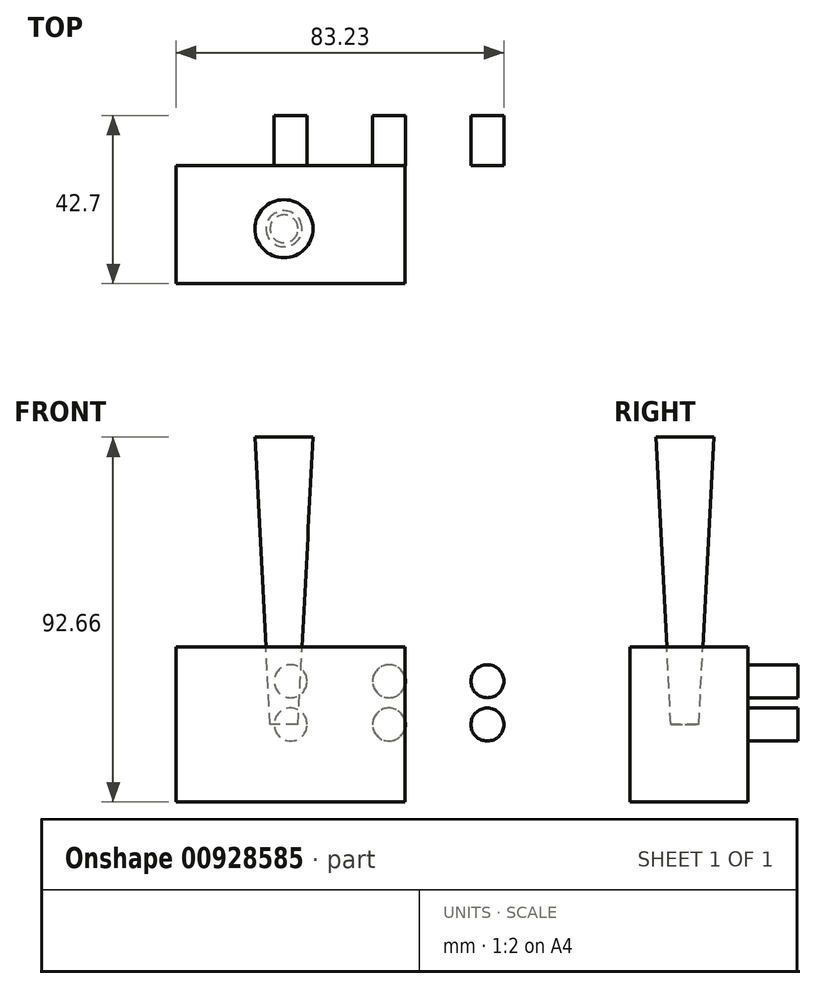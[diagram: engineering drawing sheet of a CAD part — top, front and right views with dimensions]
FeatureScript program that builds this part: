
annotation { "Feature Type Name" : "Feature", "Feature Type Description" : "" }
export const myFeature = defineFeature(function(context is Context, id is Id, definition is map)
    precondition{}
    {
        {
            var Q0;
            Q0=qCreatedBy(makeId("Front.planeOp"),FACE);
            var sketch = newSketch(context, id + "F0", { "sketchPlane" : qUnion([Q0])});
            skLineSegment(sketch, "E0.bottom", {"start": v(29.04, -19.66) * mm, "end": v(-29.04, -19.66) * mm});
            skLineSegment(sketch, "E0.top", {"start": v(29.04, 19.66) * mm, "end": v(-29.04, 19.66) * mm});
            skLineSegment(sketch, "E0.left", {"start": v(29.04, -19.66) * mm, "end": v(29.04, 19.66) * mm});
            skLineSegment(sketch, "E0.right", {"start": v(-29.04, -19.66) * mm, "end": v(-29.04, 19.66) * mm});
            skPoint(sketch, "E0.middle", {"position": v(0, 0) * mm});
            skSolve(sketch);
        }
        {
            var Q0;
            Q0 = qSketchRegion(id + "F0", true);
            extrude(context, id + "F1", {"entities" : qUnion([Q0]), "depth" : 30 * mm, "offsetDistance" : 25 * mm});
        }
        {
            var Q0;
            Q0=qCreatedBy(makeId("Front.planeOp"),FACE);
            var sketch = newSketch(context, id + "F2", { "sketchPlane" : qUnion([Q0])});
            skCircle(sketch, "E1", {"center": v(0, 0) * mm, "radius": 4.19 * mm});
            skCircle(sketch, "E2.0.1.0", {"center": v(0, 11) * mm, "radius": 4.19 * mm});
            skCircle(sketch, "E2.1.0.0", {"center": v(25, 0) * mm, "radius": 4.19 * mm});
            skCircle(sketch, "E2.1.1.0", {"center": v(25, 11) * mm, "radius": 4.19 * mm});
            skCircle(sketch, "E2.2.0.0", {"center": v(50, 0) * mm, "radius": 4.19 * mm});
            skCircle(sketch, "E2.2.1.0", {"center": v(50, 11) * mm, "radius": 4.19 * mm});
            skLineSegment(sketch, "E2.direction1", {"start": v(0, 0) * mm, "end": v(25, 0) * mm, "construction": true});
            skLineSegment(sketch, "E2.direction2", {"start": v(0, 0) * mm, "end": v(0, 11) * mm, "construction": true});
            skSolve(sketch);
        }
        {
            var Q0;
            Q0 = qSketchRegion(id + "F2", true);
            extrude(context, id + "F3", {"entities" : qUnion([Q0]), "oppositeDirection" : true, "depth" : 12.7 * mm, "offsetDistance" : 25 * mm});
        }
        {
            var Q0;
            Q0=qCreatedBy(makeId("Top.planeOp"),FACE);
            var sketch = newSketch(context, id + "F4", { "sketchPlane" : qUnion([Q0])});
            skCircle(sketch, "E3", {"center": v(-1.67, -16.04) * mm, "radius": 3.55 * mm});
            skSolve(sketch);
        }
        {
            var Q0;
            Q0 = qSketchRegion(id + "F4", true);
            extrude(context, id + "F5", {"entities" : qUnion([Q0]), "depth" : 73 * mm, "offsetDistance" : 25 * mm, "hasDraft" : true, "draftAngle" : 3 * degree});
        }
        {
            var Q0;
            Q0=makeQuery(id+"F5.opExtrude","SWEPT_BODY",BODY,{"disambiguationData":[OSD([sQuery(id+"F4.wireOp",EDGE,"E3")])]});
            var Q1;
            Q1=makeQuery(id+"F1.opExtrude","SWEPT_BODY",BODY,{"disambiguationData":[OSD([sQuery(id+"F0.wireOp",EDGE,"E0.bottom"),sQuery(id+"F0.wireOp",EDGE,"E0.top"),sQuery(id+"F0.wireOp",EDGE,"E0.left"),sQuery(id+"F0.wireOp",EDGE,"E0.right")])]});
            booleanBodies(context, id + "F6", {"operationType" : BooleanOperationType.SUBTRACTION, "tools" : qUnion([Q0]), "targets" : qUnion([Q1]), "keepTools" : true});
        }
    });
